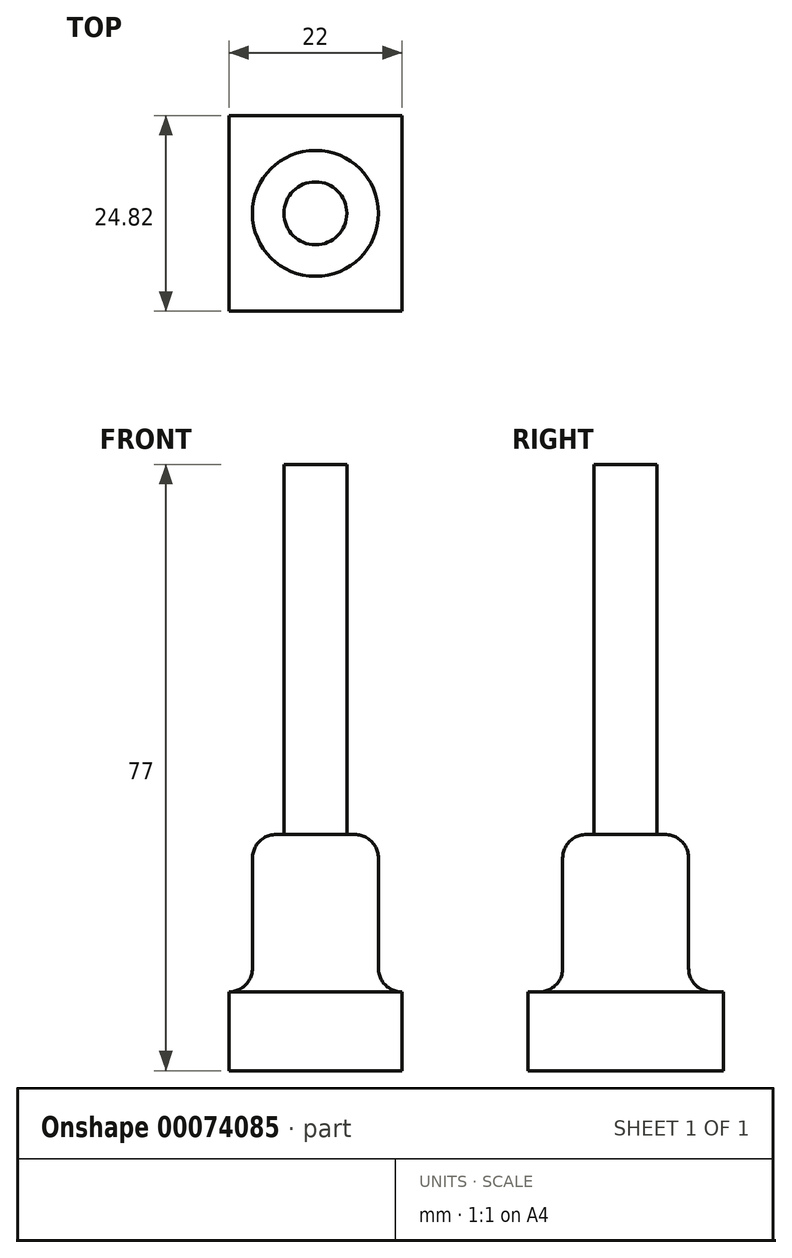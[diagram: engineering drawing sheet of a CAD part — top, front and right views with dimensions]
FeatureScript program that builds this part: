
annotation { "Feature Type Name" : "Feature", "Feature Type Description" : "" }
export const myFeature = defineFeature(function(context is Context, id is Id, definition is map)
    precondition{}
    {
        {
            var Q0;
            Q0=qCreatedBy(makeId("Top.planeOp"),FACE);
            var sketch = newSketch(context, id + "F0", { "sketchPlane" : qUnion([Q0])});
            skLineSegment(sketch, "E0.rect.bottom", {"start": v(-11, 12.4) * mm, "end": v(11, 12.4) * mm});
            skLineSegment(sketch, "E0.rect.top", {"start": v(-11, -12.4) * mm, "end": v(11, -12.4) * mm});
            skLineSegment(sketch, "E0.rect.left", {"start": v(-11, 12.4) * mm, "end": v(-11, -12.4) * mm});
            skLineSegment(sketch, "E0.rect.right", {"start": v(11, 12.4) * mm, "end": v(11, -12.4) * mm});
            skPoint(sketch, "E0.rect.middle", {"position": v(0, 0) * mm});
            skSolve(sketch);
        }
        {
            var Q0;
            Q0=makeQuery(id+"F0.imprint","IMPRINT",FACE,{"disambiguationData":[TD([[makeQuery(id+"F0.imprint","IMPRINT",EDGE,{"derivedFrom":sQuery(id+"F0.wireOp",EDGE,"E0.rect.bottom")}),-1.0]])]});
            extrude(context, id + "F1", {"entities" : qUnion([Q0]), "depth" : 10 * mm});
        }
        {
            var Q0;
            Q0=makeQuery(id+"F1.opExtrude","CAP_FACE",FACE,{"disambiguationData":[OSD([sQuery(id+"F0.wireOp",EDGE,"E0.rect.bottom"),sQuery(id+"F0.wireOp",EDGE,"E0.rect.top"),sQuery(id+"F0.wireOp",EDGE,"E0.rect.left"),sQuery(id+"F0.wireOp",EDGE,"E0.rect.right")])],"isStart":false});
            var sketch = newSketch(context, id + "F2", { "sketchPlane" : qUnion([Q0])});
            skCircle(sketch, "E1", {"center": v(0, 0) * mm, "radius": 8 * mm});
            skSolve(sketch);
        }
        {
            var Q0;
            Q0=makeQuery(id+"F2.imprint","IMPRINT",FACE,{"disambiguationData":[TD([[makeQuery(id+"F2.imprint","IMPRINT",EDGE,{"derivedFrom":sQuery(id+"F2.wireOp",EDGE,"E1")}),1.0]])]});
            extrude(context, id + "F3", {"entities" : qUnion([Q0]), "operationType" : NewBodyOperationType.ADD, "depth" : 20 * mm});
        }
        {
            var Q0;
            Q0=makeQuery(id+"F3.opExtrude","CAP_FACE",FACE,{"disambiguationData":[OSD([sQuery(id+"F2.wireOp",EDGE,"E1")])],"isStart":false});
            var sketch = newSketch(context, id + "F4", { "sketchPlane" : qUnion([Q0])});
            skCircle(sketch, "E2", {"center": v(0, 0) * mm, "radius": 4 * mm});
            skCircle(sketch, "E3", {"center": v(0, 0) * mm, "radius": 5.04 * mm});
            skSolve(sketch);
        }
        {
            var Q0;
            Q0=makeQuery(id+"F4.imprint","IMPRINT",FACE,{"disambiguationData":[TD([[makeQuery(id+"F4.imprint","IMPRINT",EDGE,{"derivedFrom":sQuery(id+"F4.wireOp",EDGE,"E2")}),1.0]])]});
            extrude(context, id + "F5", {"entities" : qUnion([Q0]), "operationType" : NewBodyOperationType.ADD, "depth" : 47 * mm});
        }
        {
            var Q0;
            Q0=makeQuery(id+"F3.opExtrude","SWEPT_FACE",FACE,{"disambiguationData":[OSD([sQuery(id+"F2.wireOp",EDGE,"E1")])]});
            fillet(context, id + "F6", {"entities" : qUnion([Q0]), "radius" : 3 * mm, "tangentPropagation" : true, "allowEdgeOverflow" : false});
        }
    });
